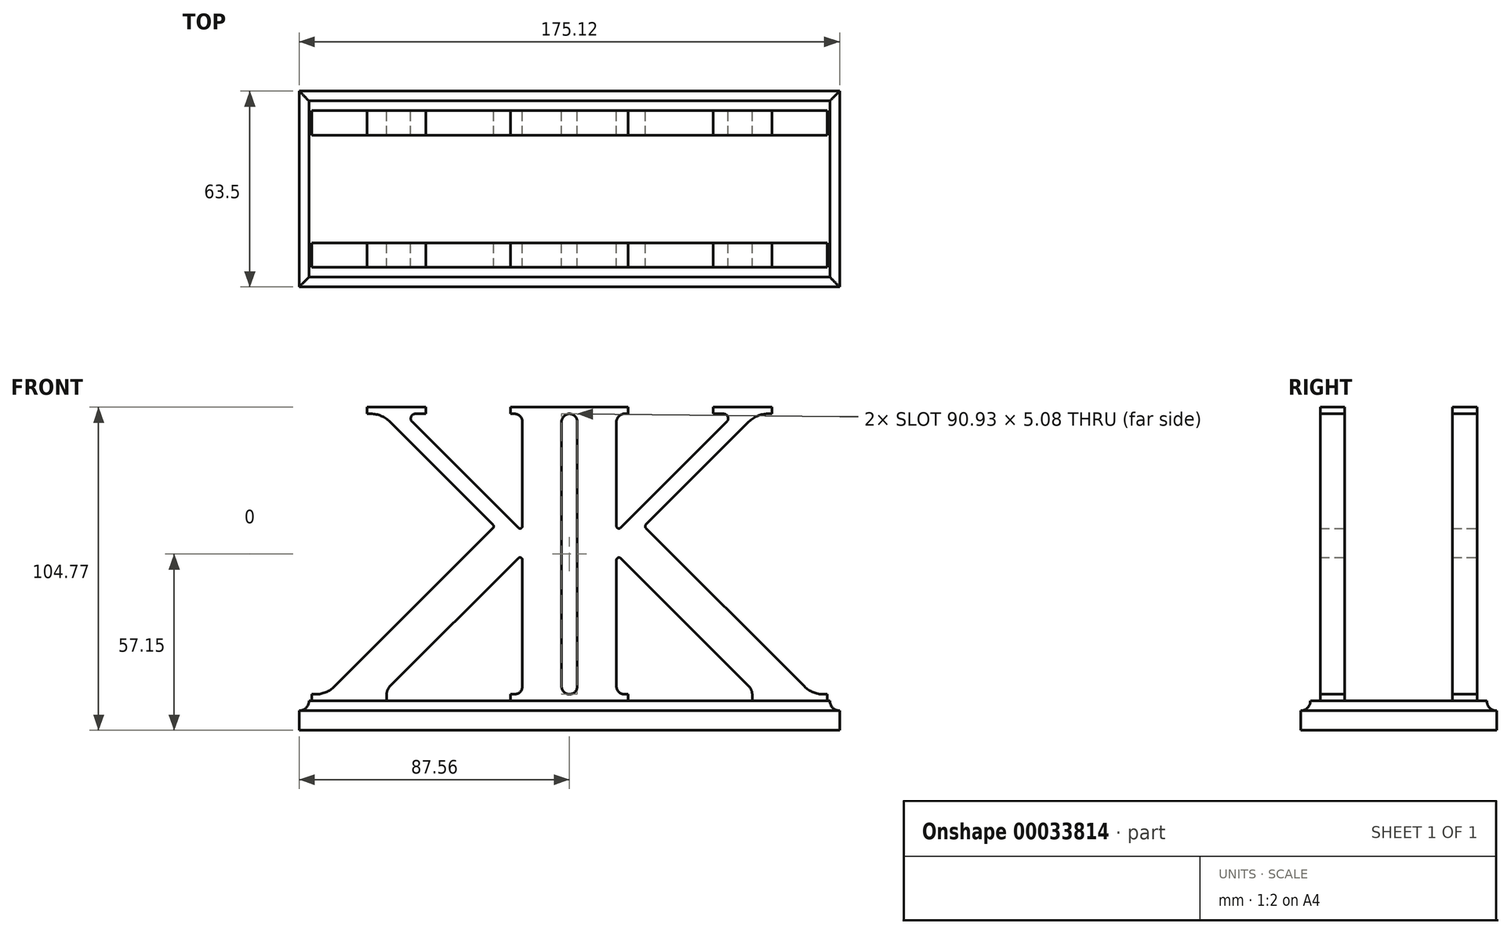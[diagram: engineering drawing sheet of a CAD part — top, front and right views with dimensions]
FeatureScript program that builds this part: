
annotation { "Feature Type Name" : "Feature", "Feature Type Description" : "" }
export const myFeature = defineFeature(function(context is Context, id is Id, definition is map)
    precondition{}
    {
        {
            var Q0;
            Q0=qCreatedBy(makeId("Front.planeOp"),FACE);
            var sketch = newSketch(context, id + "F0", { "sketchPlane" : qUnion([Q0])});
            skLineSegment(sketch, "E0.left", {"start": v(2.54, 42.93) * mm, "end": v(2.54, -42.93) * mm});
            skLineSegment(sketch, "E0.right", {"start": v(15.24, 42.93) * mm, "end": v(15.24, 9.1) * mm});
            skLineSegment(sketch, "E1", {"start": v(0, 0) * mm, "end": v(0, -47.63) * mm, "construction": true});
            skLineSegment(sketch, "E2", {"start": v(0, 47.63) * mm, "end": v(19.05, 47.63) * mm});
            skLineSegment(sketch, "E3", {"start": v(19.05, 47.63) * mm, "end": v(19.05, 45.47) * mm});
            skLineSegment(sketch, "E4", {"start": v(16.6, 8.54) * mm, "end": v(50.98, 42.93) * mm});
            skLineSegment(sketch, "E5.0", {"start": v(24.78, 9.54) * mm, "end": v(58.17, 42.93) * mm});
            skLineSegment(sketch, "E6", {"start": v(58.17, -42.93) * mm, "end": v(16.6, -1.36) * mm});
            skLineSegment(sketch, "E7.0", {"start": v(76.13, -42.93) * mm, "end": v(24.78, 8.42) * mm});
            skLineSegment(sketch, "E8", {"start": v(15.24, 42.93) * mm, "end": v(83.53, 42.93) * mm, "construction": true});
            skLineSegment(sketch, "E9", {"start": v(83.53, 42.93) * mm, "end": v(83.53, -42.93) * mm, "construction": true});
            skLineSegment(sketch, "E10", {"start": v(15.24, -42.93) * mm, "end": v(83.53, -42.93) * mm, "construction": true});
            skLineSegment(sketch, "E11", {"start": v(0, 0) * mm, "end": v(2.54, 0) * mm});
            skLineSegment(sketch, "E12", {"start": v(19.05, 45.47) * mm, "end": v(17.78, 45.47) * mm});
            skArc(sketch, "E13", {"start": v(17.78, 45.47) * mm, "mid": v(15.98, 44.72) * mm, "end": v(15.24, 42.93) * mm});
            skArc(sketch, "E14", {"start": v(2.54, 42.93) * mm, "mid": v(1.8, 44.72) * mm, "end": v(0, 45.47) * mm});
            skLineSegment(sketch, "E15", {"start": v(0, 45.47) * mm, "end": v(17.78, 45.47) * mm, "construction": true});
            skArc(sketch, "E16", {"start": v(64.3, 45.47) * mm, "mid": v(60.98, 44.8) * mm, "end": v(58.17, 42.93) * mm});
            skLineSegment(sketch, "E17", {"start": v(65.57, 45.47) * mm, "end": v(64.3, 45.47) * mm});
            skLineSegment(sketch, "E18", {"start": v(46.52, 47.63) * mm, "end": v(65.57, 47.63) * mm});
            skLineSegment(sketch, "E19", {"start": v(65.57, 47.63) * mm, "end": v(65.57, 45.47) * mm});
            skLineSegment(sketch, "E20", {"start": v(46.52, 45.47) * mm, "end": v(64.3, 45.47) * mm, "construction": true});
            skLineSegment(sketch, "E21", {"start": v(19.05, 47.63) * mm, "end": v(46.52, 47.63) * mm, "construction": true});
            skLineSegment(sketch, "E22", {"start": v(46.52, 47.63) * mm, "end": v(46.52, 45.47) * mm});
            skLineSegment(sketch, "E23.trimOffspring", {"start": v(15.24, -1.92) * mm, "end": v(15.24, -42.93) * mm});
            skLineSegment(sketch, "E24.MirrorCS", {"start": v(19.05, -47.63) * mm, "end": v(19.05, -45.47) * mm});
            skArc(sketch, "E25.MirrorCS", {"start": v(17.78, -45.47) * mm, "mid": v(15.98, -44.72) * mm, "end": v(15.24, -42.93) * mm});
            skArc(sketch, "E26.MirrorCS", {"start": v(2.54, -42.93) * mm, "mid": v(1.8, -44.72) * mm, "end": v(0, -45.47) * mm});
            skLineSegment(sketch, "E27.MirrorCS", {"start": v(0, -47.63) * mm, "end": v(19.05, -47.63) * mm});
            skLineSegment(sketch, "E28.MirrorCS", {"start": v(19.05, -45.47) * mm, "end": v(17.78, -45.47) * mm});
            skLineSegment(sketch, "E29", {"start": v(19.05, -47.63) * mm, "end": v(59.22, -47.63) * mm, "construction": true});
            skPoint(sketch, "E29.endSnap0", {"position": v(59.22, 46.96) * mm});
            skLineSegment(sketch, "E30", {"start": v(46.52, 45.47) * mm, "end": v(49.93, 45.47) * mm});
            skArc(sketch, "E31", {"start": v(50.98, 42.93) * mm, "mid": v(51.3, 44.55) * mm, "end": v(49.93, 45.47) * mm});
            skLineSegment(sketch, "E32", {"start": v(82.26, -45.47) * mm, "end": v(83.53, -45.47) * mm});
            skLineSegment(sketch, "E33", {"start": v(83.53, -45.47) * mm, "end": v(83.53, -47.62) * mm});
            skLineSegment(sketch, "E34", {"start": v(83.53, -47.63) * mm, "end": v(59.22, -47.63) * mm});
            skLineSegment(sketch, "E35", {"start": v(59.22, -47.62) * mm, "end": v(59.22, -45.47) * mm});
            skArc(sketch, "E36", {"start": v(59.22, -45.47) * mm, "mid": v(58.94, -44.1) * mm, "end": v(58.17, -42.93) * mm});
            skArc(sketch, "E37", {"start": v(76.13, -42.93) * mm, "mid": v(78.94, -44.8) * mm, "end": v(82.26, -45.47) * mm});
            skLineSegment(sketch, "E38", {"start": v(83.53, -42.93) * mm, "end": v(83.53, -45.47) * mm, "construction": true});
            skLineSegment(sketch, "E39.MirrorCS", {"start": v(-83.53, -45.47) * mm, "end": v(-83.53, -47.62) * mm});
            skLineSegment(sketch, "E40.MirrorCS", {"start": v(-59.22, -47.62) * mm, "end": v(-59.22, -45.47) * mm});
            skLineSegment(sketch, "E41.MirrorCS", {"start": v(-46.52, 45.47) * mm, "end": v(-49.93, 45.47) * mm});
            skLineSegment(sketch, "E42.MirrorCS", {"start": v(-19.05, 47.63) * mm, "end": v(-19.05, 45.47) * mm});
            skLineSegment(sketch, "E43.MirrorCS", {"start": v(-19.05, -47.63) * mm, "end": v(-19.05, -45.47) * mm});
            skLineSegment(sketch, "E44.MirrorCS", {"start": v(-46.52, 47.63) * mm, "end": v(-46.52, 45.47) * mm});
            skArc(sketch, "E45.MirrorCS", {"start": v(-50.98, 42.93) * mm, "mid": v(-51.3, 44.55) * mm, "end": v(-49.93, 45.47) * mm});
            skLineSegment(sketch, "E46.MirrorCS", {"start": v(-65.57, 47.63) * mm, "end": v(-65.57, 45.47) * mm});
            skArc(sketch, "E47.MirrorCS", {"start": v(-2.54, 42.93) * mm, "mid": v(-1.8, 44.72) * mm, "end": v(0, 45.47) * mm});
            skLineSegment(sketch, "E48.MirrorCS", {"start": v(-82.26, -45.47) * mm, "end": v(-83.53, -45.47) * mm});
            skArc(sketch, "E49.MirrorCS", {"start": v(-17.78, -45.47) * mm, "mid": v(-15.98, -44.72) * mm, "end": v(-15.24, -42.93) * mm});
            skArc(sketch, "E50.MirrorCS", {"start": v(-59.22, -45.47) * mm, "mid": v(-58.94, -44.1) * mm, "end": v(-58.17, -42.93) * mm});
            skArc(sketch, "E51.MirrorCS", {"start": v(-2.54, -42.93) * mm, "mid": v(-1.8, -44.72) * mm, "end": v(0, -45.47) * mm});
            skArc(sketch, "E52.MirrorCS", {"start": v(-64.3, 45.47) * mm, "mid": v(-60.98, 44.8) * mm, "end": v(-58.17, 42.93) * mm});
            skLineSegment(sketch, "E53.MirrorCS", {"start": v(-24.78, 9.54) * mm, "end": v(-58.17, 42.93) * mm});
            skLineSegment(sketch, "E54.MirrorCS", {"start": v(-19.05, -45.47) * mm, "end": v(-17.78, -45.47) * mm});
            skLineSegment(sketch, "E55.MirrorCS", {"start": v(-76.13, -42.93) * mm, "end": v(-24.78, 8.42) * mm});
            skLineSegment(sketch, "E56.MirrorCS", {"start": v(-58.17, -42.93) * mm, "end": v(-16.6, -1.36) * mm});
            skLineSegment(sketch, "E57.MirrorCS", {"start": v(-15.24, 42.93) * mm, "end": v(-15.24, 9.1) * mm});
            skLineSegment(sketch, "E58.MirrorCS", {"start": v(0, 47.63) * mm, "end": v(-19.05, 47.63) * mm});
            skLineSegment(sketch, "E59.MirrorCS", {"start": v(-2.54, 42.93) * mm, "end": v(-2.54, -42.93) * mm});
            skArc(sketch, "E60.MirrorCS", {"start": v(-76.13, -42.93) * mm, "mid": v(-78.94, -44.8) * mm, "end": v(-82.26, -45.47) * mm});
            skLineSegment(sketch, "E61.MirrorCS", {"start": v(-65.57, 45.47) * mm, "end": v(-64.3, 45.47) * mm});
            skLineSegment(sketch, "E62.MirrorCS", {"start": v(-46.52, 47.63) * mm, "end": v(-65.57, 47.63) * mm});
            skLineSegment(sketch, "E63.MirrorCS", {"start": v(-83.53, -47.63) * mm, "end": v(-59.22, -47.63) * mm});
            skLineSegment(sketch, "E64.MirrorCS", {"start": v(-19.05, 45.47) * mm, "end": v(-17.78, 45.47) * mm});
            skArc(sketch, "E65.MirrorCS", {"start": v(-17.78, 45.47) * mm, "mid": v(-15.98, 44.72) * mm, "end": v(-15.24, 42.93) * mm});
            skLineSegment(sketch, "E66.MirrorCS", {"start": v(0, -47.63) * mm, "end": v(-19.05, -47.63) * mm});
            skLineSegment(sketch, "E67.MirrorCS", {"start": v(-15.24, -1.92) * mm, "end": v(-15.24, -42.93) * mm});
            skLineSegment(sketch, "E68", {"start": v(0, 0) * mm, "end": v(0, 47.63) * mm, "construction": true});
            skPoint(sketch, "E69.visualSharp", {"position": v(15.24, 7.18) * mm});
            skArc(sketch, "E69.filletArc", {"start": v(15.24, 9.1) * mm, "mid": v(15.73, 8.37) * mm, "end": v(16.6, 8.54) * mm});
            skPoint(sketch, "E70.visualSharp", {"position": v(24.22, 8.98) * mm});
            skArc(sketch, "E70.filletArc", {"start": v(24.78, 9.54) * mm, "mid": v(24.55, 8.98) * mm, "end": v(24.78, 8.42) * mm});
            skPoint(sketch, "E71.visualSharp", {"position": v(15.24, 0) * mm});
            skArc(sketch, "E71.filletArc", {"start": v(16.6, -1.36) * mm, "mid": v(15.73, -1.18) * mm, "end": v(15.24, -1.92) * mm});
            skArc(sketch, "E72.MirrorCS", {"start": v(-16.6, -1.36) * mm, "mid": v(-15.73, -1.18) * mm, "end": v(-15.24, -1.92) * mm});
            skArc(sketch, "E73.MirrorCS", {"start": v(-24.78, 9.54) * mm, "mid": v(-24.55, 8.98) * mm, "end": v(-24.78, 8.42) * mm});
            skArc(sketch, "E74.MirrorCS", {"start": v(-15.24, 9.1) * mm, "mid": v(-15.73, 8.37) * mm, "end": v(-16.6, 8.54) * mm});
            skLineSegment(sketch, "E75", {"start": v(-50.98, 42.93) * mm, "end": v(-16.6, 8.54) * mm});
            skLineSegment(sketch, "E76", {"start": v(62.4, -47.63) * mm, "end": v(62.4, -50.8) * mm});
            skLineSegment(sketch, "E77", {"start": v(62.4, -50.8) * mm, "end": v(78.27, -50.8) * mm});
            skLineSegment(sketch, "E78", {"start": v(78.27, -50.8) * mm, "end": v(78.27, -47.63) * mm});
            skLineSegment(sketch, "E79.MirrorCS", {"start": v(-78.27, -50.8) * mm, "end": v(-78.27, -47.63) * mm});
            skLineSegment(sketch, "E80.MirrorCS", {"start": v(-62.4, -50.8) * mm, "end": v(-78.27, -50.8) * mm});
            skLineSegment(sketch, "E81.MirrorCS", {"start": v(-62.4, -47.63) * mm, "end": v(-62.4, -50.8) * mm});
            skSolve(sketch);
        }
        {
            var Q0;
            Q0=makeQuery(id+"F0.imprint","IMPRINT",FACE,{"disambiguationData":[TD([[makeQuery(id+"F0.imprint","IMPRINT",EDGE,{"derivedFrom":sQuery(id+"F0.wireOp",EDGE,"E0.right")}),-1.0]])]});
            extrude(context, id + "F1", {"entities" : qUnion([Q0]), "depth" : 7.94 * mm});
        }
        {
            var Q0;
            Q0=makeQuery(id+"F0.imprint","IMPRINT",FACE,{"disambiguationData":[TD([[makeQuery(id+"F0.imprint","IMPRINT",EDGE,{"derivedFrom":sQuery(id+"F0.wireOp",EDGE,"E0.right")}),-1.0]])]});
            extrude(context, id + "F2", {"entities" : qUnion([Q0]), "depth" : 50.8 * mm, "hasSecondDirection" : true, "secondDirectionOppositeDirection" : false, "secondDirectionDepth" : 42.86 * mm});
        }
        {
            var Q0;
            Q0=qCreatedBy(makeId("Front.planeOp"),FACE);
            var sketch = newSketch(context, id + "F3", { "sketchPlane" : qUnion([Q0])});
            skLineSegment(sketch, "E82", {"start": v(0, 0) * mm, "end": v(0, -47.63) * mm, "construction": true});
            skLineSegment(sketch, "E83", {"start": v(0, -47.63) * mm, "end": v(84.38, -47.63) * mm});
            skLineSegment(sketch, "E84", {"start": v(87.56, -50.8) * mm, "end": v(87.56, -57.15) * mm});
            skLineSegment(sketch, "E85", {"start": v(87.56, -57.15) * mm, "end": v(0, -57.15) * mm});
            skLineSegment(sketch, "E86.MirrorCS", {"start": v(0, -47.63) * mm, "end": v(-84.38, -47.63) * mm});
            skLineSegment(sketch, "E87.MirrorCS", {"start": v(-87.56, -57.15) * mm, "end": v(0, -57.15) * mm});
            skLineSegment(sketch, "E88.MirrorCS", {"start": v(-87.56, -50.8) * mm, "end": v(-87.56, -57.15) * mm});
            skArc(sketch, "E89", {"start": v(84.38, -47.62) * mm, "mid": v(85.31, -49.87) * mm, "end": v(87.56, -50.8) * mm});
            skArc(sketch, "E90.MirrorCS", {"start": v(-84.38, -47.62) * mm, "mid": v(-85.31, -49.87) * mm, "end": v(-87.56, -50.8) * mm});
            skPoint(sketch, "E91.orphan", {"position": v(-87.56, -47.63) * mm});
            skSolve(sketch);
        }
        {
            var Q0;
            Q0=makeQuery(id+"F3.imprint","IMPRINT",FACE,{"disambiguationData":[TD([[makeQuery(id+"F3.imprint","IMPRINT",EDGE,{"derivedFrom":sQuery(id+"F3.wireOp",EDGE,"E83")}),-1.0]])]});
            extrude(context, id + "F4", {"entities" : qUnion([Q0]), "depth" : 57.15 * mm, "hasSecondDirection" : true, "secondDirectionOppositeDirection" : true, "secondDirectionDepth" : 6.35 * mm});
        }
        {
            var Q0;
            Q0=qCreatedBy(makeId("Right.planeOp"),FACE);
            var sketch = newSketch(context, id + "F5", { "sketchPlane" : qUnion([Q0])});
            skPoint(sketch, "E92", {"position": v(6.35, -47.63) * mm});
            skCircle(sketch, "E93", {"center": v(6.35, -47.63) * mm, "radius": 3.18 * mm});
            skLineSegment(sketch, "E94", {"start": v(-25.4, 0) * mm, "end": v(-25.4, -10.84) * mm, "construction": true});
            skCircle(sketch, "E95.MirrorC", {"center": v(-57.15, -47.63) * mm, "radius": 3.18 * mm});
            skSolve(sketch);
        }
        {
            var Q0;
            Q0 = qSketchRegion(id + "F5", true);
            var Q1;
            Q1=sQuery(id+"F5.wireOp",EDGE,"E94");
            var Q2;
            Q2=sQuery(id+"F5.wireOp",EDGE,"E93");
            var Q3;
            Q3=sQuery(id+"F5.wireOp",EDGE,"E95.MirrorC");
            var Q4;
            Q4=makeQuery(id+"F4.opExtrude","SWEPT_FACE",FACE,{"disambiguationData":[OSD([sQuery(id+"F3.wireOp",EDGE,"E84")])]});
            var Q5;
            Q5=makeQuery(id+"F4.opExtrude","SWEPT_FACE",FACE,{"disambiguationData":[OSD([sQuery(id+"F3.wireOp",EDGE,"E88.MirrorCS")])]});
            extrude(context, id + "F6", {"entities" : qUnion([Q0]), "operationType" : NewBodyOperationType.REMOVE, "surfaceEntities" : qUnion([Q1, Q2, Q3]), "endBound" : BoundingType.UP_TO_SURFACE, "endBoundEntityFace" : qUnion([Q4]), "depth" : 25.4 * mm, "hasSecondDirection" : true, "secondDirectionBound" : SecondDirectionBoundingType.UP_TO_SURFACE, "secondDirectionOppositeDirection" : true, "secondDirectionBoundEntityFace" : qUnion([Q5]), "secondDirectionDepth" : 25.4 * mm});
        }
        {
            var Q0;
            {var subQ1=sQuery(id+"F0.wireOp",EDGE,"E79.MirrorCS");Q0=makeQuery(id+"F0.imprint","IMPRINT",FACE,{"disambiguationData":[TD([[makeQuery(id+"F0.imprint","IMPRINT",EDGE,{"derivedFrom":subQ1}),-1.0]])]});}
            var Q1;
            {var subQ1=sQuery(id+"F0.wireOp",EDGE,"E76");Q1=makeQuery(id+"F0.imprint","IMPRINT",FACE,{"disambiguationData":[TD([[makeQuery(id+"F0.imprint","IMPRINT",EDGE,{"derivedFrom":subQ1}),1.0]])]});}
            extrude(context, id + "F7", {"entities" : qUnion([Q0, Q1]), "operationType" : NewBodyOperationType.ADD, "depth" : 5.56 * mm, "hasSecondDirection" : true, "secondDirectionOppositeDirection" : false, "secondDirectionDepth" : 2.38 * mm});
        }
        {
            var Q0;
            {var subQ1=sQuery(id+"F0.wireOp",EDGE,"E76");Q0=makeQuery(id+"F0.imprint","IMPRINT",FACE,{"disambiguationData":[TD([[makeQuery(id+"F0.imprint","IMPRINT",EDGE,{"derivedFrom":subQ1}),1.0]])]});}
            var Q1;
            {var subQ1=sQuery(id+"F0.wireOp",EDGE,"E79.MirrorCS");Q1=makeQuery(id+"F0.imprint","IMPRINT",FACE,{"disambiguationData":[TD([[makeQuery(id+"F0.imprint","IMPRINT",EDGE,{"derivedFrom":subQ1}),-1.0]])]});}
            extrude(context, id + "F8", {"entities" : qUnion([Q0, Q1]), "operationType" : NewBodyOperationType.ADD, "depth" : 48.42 * mm, "hasSecondDirection" : true, "secondDirectionOppositeDirection" : false, "secondDirectionDepth" : 45.24 * mm});
        }
    });
